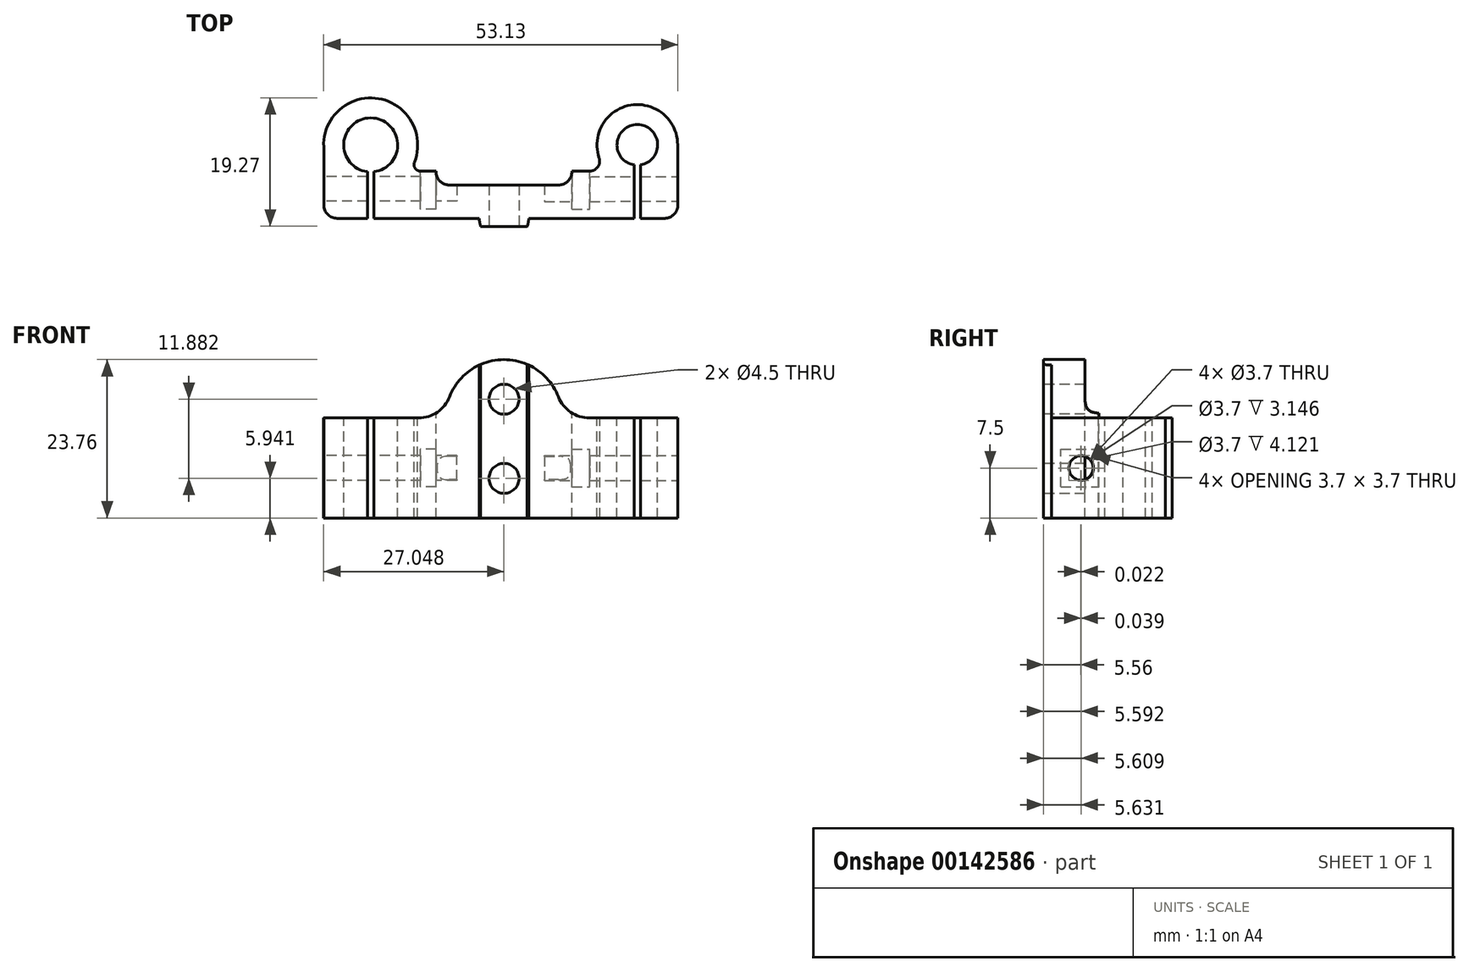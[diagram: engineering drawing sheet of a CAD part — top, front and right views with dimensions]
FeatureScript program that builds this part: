
annotation { "Feature Type Name" : "Feature", "Feature Type Description" : "" }
export const myFeature = defineFeature(function(context is Context, id is Id, definition is map)
    precondition{}
    {
        {
            var Q0;
            Q0=qCreatedBy(makeId("Top.planeOp"),FACE);
            var sketch = newSketch(context, id + "F0", { "sketchPlane" : qUnion([Q0])});
            skArc(sketch, "E0", {"start": v(12.6, -22.52) * mm, "mid": v(12.1, -16.46) * mm, "end": v(11.6, -22.52) * mm});
            skArc(sketch, "E1", {"start": v(-27.4, -23.53) * mm, "mid": v(-27.9, -15.46) * mm, "end": v(-28.4, -23.53) * mm});
            skArc(sketch, "E2", {"start": v(18.16, -19.49) * mm, "mid": v(11.1, -13.55) * mm, "end": v(6.38, -21.47) * mm});
            skArc(sketch, "E3", {"start": v(-21.33, -22.1) * mm, "mid": v(-26.72, -12.56) * mm, "end": v(-34.94, -19.8) * mm});
            skLineSegment(sketch, "E4", {"start": v(0.3, -25.53) * mm, "end": v(-16.08, -25.53) * mm});
            skLineSegment(sketch, "E5", {"start": v(-32.94, -30.53) * mm, "end": v(-28.4, -30.53) * mm});
            skLineSegment(sketch, "E6", {"start": v(-34.94, -19.8) * mm, "end": v(-34.94, -28.53) * mm});
            skPoint(sketch, "E7", {"position": v(-8.2, -30.53) * mm});
            skPoint(sketch, "E8", {"position": v(-8.2, -25.53) * mm});
            skLineSegment(sketch, "E9.rect.top", {"start": v(-27.4, -8.5) * mm, "end": v(-28.4, -8.5) * mm});
            skLineSegment(sketch, "E9.rect.left", {"start": v(-27.4, -30.53) * mm, "end": v(-27.4, -23.53) * mm});
            skLineSegment(sketch, "E9.rect.right", {"start": v(-28.4, -30.53) * mm, "end": v(-28.4, -23.53) * mm});
            skLineSegment(sketch, "E10.MirrorCS", {"start": v(-26.83, -5.34) * mm, "end": v(-27.83, -5.34) * mm});
            skLineSegment(sketch, "E11", {"start": v(-27.9, -19.51) * mm, "end": v(12.1, -19.51) * mm, "construction": true});
            skPoint(sketch, "E12", {"position": v(-7.9, -19.51) * mm});
            skLineSegment(sketch, "E13", {"start": v(-7.9, -19.51) * mm, "end": v(-7.9, -30.53) * mm, "construction": true});
            skLineSegment(sketch, "E14.MirrorCS", {"start": v(11.04, -5.34) * mm, "end": v(12.04, -5.34) * mm});
            skLineSegment(sketch, "E15.MirrorCS", {"start": v(12.6, -30.53) * mm, "end": v(12.6, -22.52) * mm});
            skLineSegment(sketch, "E16.MirrorCS", {"start": v(11.6, -30.53) * mm, "end": v(11.6, -22.52) * mm});
            skPoint(sketch, "E17.MirrorCS.end.orphan", {"position": v(12.6, -8.5) * mm});
            skPoint(sketch, "E18.orphan", {"position": v(11.6, -8.5) * mm});
            skPoint(sketch, "E19.MirrorCS.end.orphan", {"position": v(12.04, -5.34) * mm});
            skPoint(sketch, "E19.MirrorCS.start.orphan", {"position": v(11.04, -5.34) * mm});
            skLineSegment(sketch, "E20.trimOffspring", {"start": v(-27.4, -30.53) * mm, "end": v(-11.6, -30.53) * mm});
            skLineSegment(sketch, "E21.trimOffspring", {"start": v(12.6, -30.53) * mm, "end": v(16.2, -30.53) * mm});
            skLineSegment(sketch, "E22.filletArc", {"start": v(11.5, -25.53) * mm, "end": v(11.5, -25.53) * mm});
            skLineSegment(sketch, "E23.filletArc", {"start": v(-24.22, -25.53) * mm, "end": v(-24.22, -25.53) * mm});
            skPoint(sketch, "E24.orphan", {"position": v(18.12, -30.53) * mm});
            skLineSegment(sketch, "E25", {"start": v(18.2, -28.52) * mm, "end": v(18.16, -19.49) * mm});
            skPoint(sketch, "E26.orphan", {"position": v(-34.5, -30.53) * mm});
            skPoint(sketch, "E27.visualSharp", {"position": v(18.2, -30.53) * mm});
            skArc(sketch, "E27.filletArc", {"start": v(16.2, -30.53) * mm, "mid": v(17.61, -29.94) * mm, "end": v(18.2, -28.52) * mm});
            skPoint(sketch, "E28.visualSharp", {"position": v(-34.94, -30.53) * mm});
            skArc(sketch, "E28.filletArc", {"start": v(-34.94, -28.53) * mm, "mid": v(-34.35, -29.95) * mm, "end": v(-32.94, -30.53) * mm});
            skLineSegment(sketch, "E29.rect.bottom", {"start": v(-18.08, -28.96) * mm, "end": v(-20.58, -28.96) * mm});
            skLineSegment(sketch, "E29.rect.left", {"start": v(-18.08, -28.96) * mm, "end": v(-18.08, -25.53) * mm});
            skLineSegment(sketch, "E29.rect.right", {"start": v(-20.58, -28.96) * mm, "end": v(-20.58, -25.53) * mm});
            skPoint(sketch, "E29.rect.middle", {"position": v(-19.33, -26.2) * mm});
            skLineSegment(sketch, "E30.MirrorCS", {"start": v(4.8, -28.96) * mm, "end": v(4.8, -25.53) * mm});
            skLineSegment(sketch, "E31.MirrorCS", {"start": v(2.3, -28.96) * mm, "end": v(2.3, -25.53) * mm});
            skLineSegment(sketch, "E32.MirrorCS", {"start": v(2.3, -28.96) * mm, "end": v(4.8, -28.96) * mm});
            skPoint(sketch, "E33.MirrorP", {"position": v(3.55, -26.2) * mm});
            skPoint(sketch, "E34", {"position": v(-27.4, -27.03) * mm});
            skPoint(sketch, "E35.orphan", {"position": v(-20.58, -23.46) * mm});
            skPoint(sketch, "E36.orphan", {"position": v(-18.08, -23.46) * mm});
            skPoint(sketch, "E37.MirrorCS.end.orphan", {"position": v(4.8, -23.46) * mm});
            skPoint(sketch, "E37.MirrorCS.start.orphan", {"position": v(2.3, -23.46) * mm});
            skLineSegment(sketch, "E38", {"start": v(-20.58, -25.53) * mm, "end": v(-20.58, -23.46) * mm});
            skLineSegment(sketch, "E39", {"start": v(-18.08, -23.46) * mm, "end": v(-18.08, -23.53) * mm});
            skLineSegment(sketch, "E40", {"start": v(-20.4, -23.46) * mm, "end": v(-18.08, -23.46) * mm});
            skLineSegment(sketch, "E41", {"start": v(2.3, -23.46) * mm, "end": v(4.96, -23.46) * mm});
            skLineSegment(sketch, "E42", {"start": v(4.8, -25.53) * mm, "end": v(4.8, -23.46) * mm});
            skLineSegment(sketch, "E43", {"start": v(2.3, -23.46) * mm, "end": v(2.3, -23.53) * mm});
            skLineSegment(sketch, "E44.filletArc", {"start": v(-22.05, -23.46) * mm, "end": v(-22.05, -23.46) * mm});
            skLineSegment(sketch, "E45.filletArc", {"start": v(7.52, -23.46) * mm, "end": v(7.52, -23.46) * mm});
            skArc(sketch, "E46.filletArc", {"start": v(-21.33, -22.1) * mm, "mid": v(-21.23, -23.02) * mm, "end": v(-20.4, -23.46) * mm});
            skArc(sketch, "E47.filletArc", {"start": v(4.96, -23.46) * mm, "mid": v(6.18, -22.83) * mm, "end": v(6.38, -21.47) * mm});
            skArc(sketch, "E48.filletArc", {"start": v(-18.08, -23.53) * mm, "mid": v(-17.5, -24.95) * mm, "end": v(-16.08, -25.53) * mm});
            skArc(sketch, "E49.filletArc", {"start": v(0.3, -25.53) * mm, "mid": v(1.71, -24.95) * mm, "end": v(2.3, -23.53) * mm});
            skArc(sketch, "E50", {"start": v(-11.6, -30.53) * mm, "mid": v(-11.54, -31.14) * mm, "end": v(-11.4, -31.73) * mm});
            skLineSegment(sketch, "E51.trimOffspring", {"start": v(-4.2, -30.53) * mm, "end": v(11.6, -30.53) * mm});
            skLineSegment(sketch, "E52", {"start": v(-4.4, -31.73) * mm, "end": v(-11.4, -31.73) * mm});
            skArc(sketch, "E53.trimOffspring", {"start": v(-4.4, -31.73) * mm, "mid": v(-4.24, -31.14) * mm, "end": v(-4.2, -30.53) * mm});
            skSolve(sketch);
        }
        {
            var Q0;
            Q0=qSketchRegion(id+"F0",true);
            var Q1;
            Q1=makeQuery(id+"F0.imprint","IMPRINT",FACE,{"disambiguationData":[TD([[makeQuery(id+"F0.imprint","IMPRINT",EDGE,{"derivedFrom":sQuery(id+"F0.wireOp",EDGE,"E0")}),-1.0]])]});
            extrude(context, id + "F1", {"entities" : qUnion([Q0, Q1]), "oppositeDirection" : true, "depth" : 15 * mm});
        }
        {
            var Q0;
            Q0=qCreatedBy(makeId("Right.planeOp"),FACE);
            var sketch = newSketch(context, id + "F2", { "sketchPlane" : qUnion([Q0])});
            skLineSegment(sketch, "E54.0.0", {"start": v(-19.49, 0) * mm, "end": v(-28.52, 0) * mm});
            skLineSegment(sketch, "E54.0.1", {"start": v(-28.52, 0) * mm, "end": v(-28.52, -15) * mm});
            skLineSegment(sketch, "E54.0.2", {"start": v(-28.52, -15) * mm, "end": v(-19.49, -15) * mm});
            skLineSegment(sketch, "E54.0.3", {"start": v(-19.49, -15) * mm, "end": v(-19.49, 0) * mm});
            skLineSegment(sketch, "E54.1.0", {"start": v(-28.52, 0) * mm, "end": v(-30.53, 0) * mm});
            skLineSegment(sketch, "E54.1.1", {"start": v(-30.53, 0) * mm, "end": v(-30.53, -15) * mm});
            skLineSegment(sketch, "E54.1.2", {"start": v(-30.53, -15) * mm, "end": v(-28.52, -15) * mm});
            skLineSegment(sketch, "E54.1.3", {"start": v(-28.52, -15) * mm, "end": v(-28.52, 0) * mm});
            skPoint(sketch, "E55", {"position": v(-19.49, -7.5) * mm});
            skLineSegment(sketch, "E56", {"start": v(-19.49, -7.5) * mm, "end": v(-30.53, -7.5) * mm});
            skPoint(sketch, "E57", {"position": v(-26.2, -7.5) * mm});
            skPoint(sketch, "E58", {"position": v(-29.45, -48.71) * mm});
            skPoint(sketch, "E59", {"position": v(-22.93, -48.71) * mm});
            skPoint(sketch, "E60.trimOffspring.end.orphan", {"position": v(-22.59, -47.18) * mm});
            skPoint(sketch, "E61.trimOffspring.start.orphan", {"position": v(-29.79, -47.18) * mm});
            skSolve(sketch);
        }
        {
            var Q0;
            Q0=makeQuery(id+"F1.opExtrude","SWEPT_FACE",FACE,{"disambiguationData":[OSD([sQuery(id+"F0.wireOp",EDGE,"E25")])]});
            var sketch = newSketch(context, id + "F3", { "sketchPlane" : qUnion([Q0])});
            skPoint(sketch, "E62", {"position": v(-28.96, -7.5) * mm});
            skPoint(sketch, "E63", {"position": v(-37.59, 27.7) * mm});
            skPoint(sketch, "E64", {"position": v(-31.07, 27.7) * mm});
            skPoint(sketch, "E65.trimOffspring.end.orphan", {"position": v(-30.73, 29.23) * mm});
            skPoint(sketch, "E66.start.orphan", {"position": v(-37.93, 29.23) * mm});
            skPoint(sketch, "E67", {"position": v(-23.46, -7.5) * mm});
            skLineSegment(sketch, "E68", {"start": v(-28.9, -7.5) * mm, "end": v(-28.96, -7.5) * mm});
            skLineSegment(sketch, "E69", {"start": v(-23.44, -7.5) * mm, "end": v(-23.46, -7.5) * mm});
            skPoint(sketch, "E70", {"position": v(-26.17, -7.5) * mm});
            skCircle(sketch, "E71", {"center": v(-26.17, -7.5) * mm, "radius": 1.85 * mm});
            skPoint(sketch, "E72.0.start.orphan", {"position": v(-19.49, -7.5) * mm});
            skPoint(sketch, "E73.orphan", {"position": v(-30.53, -7.5) * mm});
            skSolve(sketch);
        }
        {
            var Q0;
            Q0=makeQuery(id+"F1.opExtrude","SWEPT_FACE",FACE,{"disambiguationData":[OSD([sQuery(id+"F0.wireOp",EDGE,"E6")])]});
            var sketch = newSketch(context, id + "F4", { "sketchPlane" : qUnion([Q0])});
            skEllipse(sketch, "E74.0", {"center": v(26.1, -7.5) * mm, "majorRadius": 1.85 * mm, "minorRadius": 1.85 * mm, "majorAxis": v(0, 1)});
            skSolve(sketch);
        }
        {
            var Q0;
            Q0=makeQuery(id+"F4.imprint","IMPRINT",FACE,{"disambiguationData":[TD([[makeQuery(id+"F4.imprint","IMPRINT",EDGE,{"derivedFrom":sQuery(id+"F4.wireOp",EDGE,"E74.0")}),1.0]])]});
            extrude(context, id + "F5", {"entities" : qUnion([Q0]), "operationType" : NewBodyOperationType.REMOVE, "oppositeDirection" : true, "depth" : 20 * mm});
        }
        {
            var Q0;
            Q0=qSketchRegion(id+"F3",true);
            var Q1;
            Q1=makeQuery(id+"F3.imprint","IMPRINT",FACE,{"disambiguationData":[TD([[makeQuery(id+"F3.imprint","IMPRINT",EDGE,{"derivedFrom":sQuery(id+"F3.wireOp",EDGE,"E71")}),1.0]])]});
            extrude(context, id + "F6", {"entities" : qUnion([Q0, Q1]), "operationType" : NewBodyOperationType.REMOVE, "oppositeDirection" : true, "depth" : 20 * mm});
        }
        {
            var Q0;
            Q0=makeQuery(id+"F1.opExtrude","SWEPT_FACE",FACE,{"disambiguationData":[OSD([sQuery(id+"F0.wireOp",EDGE,"E41")])]});
            var sketch = newSketch(context, id + "F7", { "sketchPlane" : qUnion([Q0])});
            skLineSegment(sketch, "E75", {"start": v(-2.3, -7.5) * mm, "end": v(-4.96, -7.5) * mm});
            skPoint(sketch, "E76", {"position": v(-3.63, -7.5) * mm});
            skLineSegment(sketch, "E77.rect.bottom", {"start": v(-2.3, -10.35) * mm, "end": v(-4.96, -10.35) * mm});
            skLineSegment(sketch, "E77.rect.top", {"start": v(-2.3, -4.65) * mm, "end": v(-4.96, -4.65) * mm});
            skLineSegment(sketch, "E77.rect.left", {"start": v(-2.3, -10.35) * mm, "end": v(-2.3, -4.65) * mm});
            skLineSegment(sketch, "E77.rect.right", {"start": v(-4.96, -10.35) * mm, "end": v(-4.96, -4.65) * mm});
            skLineSegment(sketch, "E78.0.0", {"start": v(20.4, 0) * mm, "end": v(18.08, 0) * mm});
            skLineSegment(sketch, "E78.0.1", {"start": v(18.08, 0) * mm, "end": v(18.08, -15) * mm});
            skLineSegment(sketch, "E78.0.2", {"start": v(18.08, -15) * mm, "end": v(20.4, -15) * mm});
            skLineSegment(sketch, "E78.0.3", {"start": v(20.4, -15) * mm, "end": v(20.4, 0) * mm});
            skLineSegment(sketch, "E79", {"start": v(-2.3, -7.5) * mm, "end": v(18.08, -7.5) * mm});
            skPoint(sketch, "E80", {"position": v(7.9, -7.5) * mm});
            skLineSegment(sketch, "E81", {"start": v(7.9, -7.5) * mm, "end": v(7.9, -15.38) * mm, "construction": true});
            skPoint(sketch, "E82.MirrorP", {"position": v(19.42, -7.5) * mm});
            skLineSegment(sketch, "E83.MirrorCS", {"start": v(18.08, -7.5) * mm, "end": v(20.75, -7.5) * mm});
            skLineSegment(sketch, "E84.MirrorCS", {"start": v(18.08, -10.35) * mm, "end": v(20.75, -10.35) * mm});
            skLineSegment(sketch, "E85.MirrorCS", {"start": v(18.08, -4.65) * mm, "end": v(20.75, -4.65) * mm});
            skLineSegment(sketch, "E86.MirrorCS", {"start": v(18.08, -10.35) * mm, "end": v(18.08, -4.65) * mm});
            skLineSegment(sketch, "E87.MirrorCS", {"start": v(18.08, -7.5) * mm, "end": v(-2.3, -7.5) * mm});
            skLineSegment(sketch, "E88.MirrorCS", {"start": v(20.75, -10.35) * mm, "end": v(20.75, -4.65) * mm});
            skSolve(sketch);
        }
        {
            var Q0;
            {var subQ0=sQuery(id+"F7.wireOp",EDGE,"E75");Q0=makeQuery(id+"F7.imprint","IMPRINT",FACE,{"disambiguationData":[TD([[makeQuery(id+"F7.imprint","IMPRINT",EDGE,{"derivedFrom":subQ0}),-1.0]])]});}
            var Q1;
            {var subQ0=sQuery(id+"F7.wireOp",EDGE,"E84.MirrorCS");var subQ1=sQuery(id+"F7.wireOp",EDGE,"E78.0.3");var subQ2=makeQuery(id+"F7.imprint","INTERSECT",VERTEX,{"derivedFrom":[subQ1,subQ0]});Q1=makeQuery(id+"F7.imprint","IMPRINT",FACE,{"disambiguationData":[TD([[makeQuery(id+"F7.imprint","IMPRINT",EDGE,{"disambiguationData":[TD([[subQ2,-1.0]])],"derivedFrom":subQ1}),1.0]])]});}
            var Q2;
            {var subQ0=sQuery(id+"F7.wireOp",EDGE,"E85.MirrorCS");var subQ1=sQuery(id+"F7.wireOp",EDGE,"E78.0.3");var subQ2=makeQuery(id+"F7.imprint","INTERSECT",VERTEX,{"derivedFrom":[subQ1,subQ0]});Q2=makeQuery(id+"F7.imprint","IMPRINT",FACE,{"disambiguationData":[TD([[makeQuery(id+"F7.imprint","IMPRINT",EDGE,{"disambiguationData":[TD([[subQ2,1.0]])],"derivedFrom":subQ1}),1.0]])]});}
            var Q3;
            {var subQ0=sQuery(id+"F7.wireOp",EDGE,"E75");Q3=makeQuery(id+"F7.imprint","IMPRINT",FACE,{"disambiguationData":[TD([[makeQuery(id+"F7.imprint","IMPRINT",EDGE,{"derivedFrom":subQ0}),1.0]])]});}
            extrude(context, id + "F8", {"entities" : qUnion([Q0, Q1, Q2, Q3]), "operationType" : NewBodyOperationType.REMOVE, "oppositeDirection" : true, "depth" : 5.7 * mm});
        }
        {
            var Q0;
            Q0=makeQuery(id+"F1.opExtrude","SWEPT_FACE",FACE,{"disambiguationData":[OSD([sQuery(id+"F0.wireOp",EDGE,"E20.trimOffspring")])]});
            var sketch = newSketch(context, id + "F9", { "sketchPlane" : qUnion([Q0])});
            skLineSegment(sketch, "E89.0.0", {"start": v(11.6, 0) * mm, "end": v(-4.2, 0) * mm});
            skLineSegment(sketch, "E89.0.1", {"start": v(-4.2, 0) * mm, "end": v(-4.2, -15) * mm});
            skLineSegment(sketch, "E89.0.2", {"start": v(-4.2, -15) * mm, "end": v(11.6, -15) * mm});
            skLineSegment(sketch, "E89.0.3", {"start": v(11.6, -15) * mm, "end": v(11.6, 0) * mm});
            skLineSegment(sketch, "E90", {"start": v(11.6, 0) * mm, "end": v(4.93, 0) * mm});
            skPoint(sketch, "E91", {"position": v(-7.9, 0) * mm});
            skArc(sketch, "E92", {"start": v(0.27, 3.18) * mm, "mid": v(-7.9, 8.76) * mm, "end": v(-16.06, 3.18) * mm});
            skLineSegment(sketch, "E93.trimOffspring", {"start": v(-20.72, 0) * mm, "end": v(-27.4, 0) * mm});
            skPoint(sketch, "E94.visualSharp", {"position": v(-16.66, 0) * mm});
            skArc(sketch, "E94.filletArc", {"start": v(-20.72, 0) * mm, "mid": v(-17.9, 0.87) * mm, "end": v(-16.06, 3.18) * mm});
            skPoint(sketch, "E95.visualSharp", {"position": v(0.87, 0) * mm});
            skArc(sketch, "E95.filletArc", {"start": v(0.27, 3.18) * mm, "mid": v(2.11, 0.87) * mm, "end": v(4.93, 0) * mm});
            skLineSegment(sketch, "E96", {"start": v(-20.72, 0) * mm, "end": v(4.93, 0) * mm});
            skSolve(sketch);
        }
        {
            var Q0;
            Q0=makeQuery(id+"F9.imprint","IMPRINT",FACE,{"disambiguationData":[TD([[makeQuery(id+"F9.imprint","IMPRINT",EDGE,{"derivedFrom":sQuery(id+"F9.wireOp",EDGE,"E92")}),1.0]])]});
            var Q1;
            Q1=makeQuery(id+"F1.opExtrude","SWEPT_FACE",FACE,{"disambiguationData":[OSD([sQuery(id+"F0.wireOp",EDGE,"E4")])]});
            extrude(context, id + "F10", {"entities" : qUnion([Q0]), "operationType" : NewBodyOperationType.ADD, "endBound" : BoundingType.UP_TO_SURFACE, "oppositeDirection" : true, "endBoundEntityFace" : qUnion([Q1]), "depth" : 25 * mm});
        }
        {
            var Q0;
            {var subQ0=sQuery(id+"F0.wireOp",EDGE,"E51.trimOffspring");var subQ1=sQuery(id+"F0.wireOp",EDGE,"E50");var subQ2=sQuery(id+"F0.wireOp",EDGE,"E52");var subQ3=sQuery(id+"F0.wireOp",EDGE,"E20.trimOffspring");var subQ4=sQuery(id+"F0.wireOp",EDGE,"E53.trimOffspring");Q0=makeQuery(id+"F10.boolean.opBoolean","SPLIT",FACE,{"disambiguationData":[TD([makeQuery(id+"F1.opExtrude","SWEPT_FACE",FACE,{"disambiguationData":[OSD([subQ1])]})])],"derivedFrom":makeQuery(id+"F1.opExtrude","CAP_FACE",FACE,{"disambiguationData":[OSD([sQuery(id+"F0.wireOp",EDGE,"E0"),sQuery(id+"F0.wireOp",EDGE,"E1"),sQuery(id+"F0.wireOp",EDGE,"E2"),sQuery(id+"F0.wireOp",EDGE,"E3"),sQuery(id+"F0.wireOp",EDGE,"E4"),sQuery(id+"F0.wireOp",EDGE,"E5"),sQuery(id+"F0.wireOp",EDGE,"E6"),sQuery(id+"F0.wireOp",EDGE,"E9.rect.left"),sQuery(id+"F0.wireOp",EDGE,"E9.rect.right"),sQuery(id+"F0.wireOp",EDGE,"E15.MirrorCS"),sQuery(id+"F0.wireOp",EDGE,"E16.MirrorCS"),subQ3,sQuery(id+"F0.wireOp",EDGE,"E21.trimOffspring"),sQuery(id+"F0.wireOp",EDGE,"E25"),sQuery(id+"F0.wireOp",EDGE,"E27.filletArc"),sQuery(id+"F0.wireOp",EDGE,"E28.filletArc"),sQuery(id+"F0.wireOp",EDGE,"E39"),sQuery(id+"F0.wireOp",EDGE,"E40"),sQuery(id+"F0.wireOp",EDGE,"E41"),sQuery(id+"F0.wireOp",EDGE,"E43"),sQuery(id+"F0.wireOp",EDGE,"E46.filletArc"),sQuery(id+"F0.wireOp",EDGE,"E47.filletArc"),sQuery(id+"F0.wireOp",EDGE,"E48.filletArc"),sQuery(id+"F0.wireOp",EDGE,"E49.filletArc"),subQ1,subQ0,subQ2,subQ4])],"isStart":true})});}
            var Q1;
            Q1=makeQuery(id+"F10.opExtrude","SWEPT_FACE",FACE,{"disambiguationData":[OSD([sQuery(id+"F9.wireOp",EDGE,"E92")])]});
            extrude(context, id + "F11", {"entities" : qUnion([Q0]), "operationType" : NewBodyOperationType.ADD, "endBound" : BoundingType.UP_TO_SURFACE, "endBoundEntityFace" : qUnion([Q1]), "depth" : 25 * mm});
        }
        {
            var Q0;
            {var subQ0=sQuery(id+"F0.wireOp",EDGE,"E52");Q0=makeQuery(id+"F11.boolean.opBoolean","MERGE",FACE,{"derivedFrom":[makeQuery(id+"F1.opExtrude","SWEPT_FACE",FACE,{"disambiguationData":[OSD([subQ0])]}),makeQuery(id+"F11.opExtrude","SWEPT_FACE",FACE,{"disambiguationData":[OSD([subQ0])]})]});}
            var sketch = newSketch(context, id + "F12", { "sketchPlane" : qUnion([Q0])});
            skLineSegment(sketch, "E97", {"start": v(-7.9, -15) * mm, "end": v(-7.9, -9.06) * mm});
            skPoint(sketch, "E98", {"position": v(-7.9, -3.12) * mm});
            skLineSegment(sketch, "E99", {"start": v(-7.9, -3.12) * mm, "end": v(-7.9, 2.82) * mm});
            skLineSegment(sketch, "E100", {"start": v(-7.9, 2.82) * mm, "end": v(-7.9, 8.76) * mm});
            skLineSegment(sketch, "E101", {"start": v(-7.9, -9.06) * mm, "end": v(-7.9, -3.12) * mm});
            skSolve(sketch);
        }
        {
            var Q0;
            Q0=sQuery(id+"F12.wireOp",VERTEX,"E100.start");
            var Q1;
            Q1=sQuery(id+"F12.wireOp",VERTEX,"E101.start");
            var Q2;
            Q2=makeQuery(id+"F1.opExtrude","SWEPT_BODY",BODY,{"disambiguationData":[OSD([sQuery(id+"F0.wireOp",EDGE,"E0"),sQuery(id+"F0.wireOp",EDGE,"E1"),sQuery(id+"F0.wireOp",EDGE,"E2"),sQuery(id+"F0.wireOp",EDGE,"E3"),sQuery(id+"F0.wireOp",EDGE,"E4"),sQuery(id+"F0.wireOp",EDGE,"E5"),sQuery(id+"F0.wireOp",EDGE,"E6"),sQuery(id+"F0.wireOp",EDGE,"E9.rect.left"),sQuery(id+"F0.wireOp",EDGE,"E9.rect.right"),sQuery(id+"F0.wireOp",EDGE,"E15.MirrorCS"),sQuery(id+"F0.wireOp",EDGE,"E16.MirrorCS"),sQuery(id+"F0.wireOp",EDGE,"E20.trimOffspring"),sQuery(id+"F0.wireOp",EDGE,"E21.trimOffspring"),sQuery(id+"F0.wireOp",EDGE,"E25"),sQuery(id+"F0.wireOp",EDGE,"E27.filletArc"),sQuery(id+"F0.wireOp",EDGE,"E28.filletArc"),sQuery(id+"F0.wireOp",EDGE,"E39"),sQuery(id+"F0.wireOp",EDGE,"E40"),sQuery(id+"F0.wireOp",EDGE,"E41"),sQuery(id+"F0.wireOp",EDGE,"E43"),sQuery(id+"F0.wireOp",EDGE,"E46.filletArc"),sQuery(id+"F0.wireOp",EDGE,"E47.filletArc"),sQuery(id+"F0.wireOp",EDGE,"E48.filletArc"),sQuery(id+"F0.wireOp",EDGE,"E49.filletArc"),sQuery(id+"F0.wireOp",EDGE,"E50"),sQuery(id+"F0.wireOp",EDGE,"E51.trimOffspring"),sQuery(id+"F0.wireOp",EDGE,"E52"),sQuery(id+"F0.wireOp",EDGE,"E53.trimOffspring")])]});
            hole(context, id + "F13", {"style" : HoleStyle.SIMPLE, "holeDiameter" : 4.5 * mm, "endStyle" : HoleEndStyle.THROUGH, "locations" : qUnion([Q0, Q1]), "scope" : qUnion([Q2])});
        }
        {
            var Q0;
            {var subQ0=sQuery(id+"F0.wireOp",EDGE,"E41");var subQ1=sQuery(id+"F0.wireOp",EDGE,"E20.trimOffspring");var subQ2=sQuery(id+"F0.wireOp",EDGE,"E25");var subQ3=sQuery(id+"F0.wireOp",EDGE,"E21.trimOffspring");var subQ4=sQuery(id+"F0.wireOp",EDGE,"E43");var subQ9=sQuery(id+"F0.wireOp",EDGE,"E16.MirrorCS");var subQ10=sQuery(id+"F0.wireOp",EDGE,"E0");var subQ11=sQuery(id+"F0.wireOp",EDGE,"E27.filletArc");var subQ12=sQuery(id+"F0.wireOp",EDGE,"E2");var subQ13=sQuery(id+"F0.wireOp",EDGE,"E4");var subQ14=sQuery(id+"F0.wireOp",EDGE,"E47.filletArc");var subQ15=sQuery(id+"F0.wireOp",EDGE,"E15.MirrorCS");var subQ16=sQuery(id+"F0.wireOp",EDGE,"E49.filletArc");var subQ17=sQuery(id+"F0.wireOp",EDGE,"E51.trimOffspring");Q0=makeQuery(id+"F10.boolean.opBoolean","SPLIT",FACE,{"disambiguationData":[TD([makeQuery(id+"F1.opExtrude","SWEPT_FACE",FACE,{"disambiguationData":[OSD([subQ10])]})])],"derivedFrom":makeQuery(id+"F1.opExtrude","CAP_FACE",FACE,{"disambiguationData":[OSD([subQ10,sQuery(id+"F0.wireOp",EDGE,"E1"),subQ12,sQuery(id+"F0.wireOp",EDGE,"E3"),subQ13,sQuery(id+"F0.wireOp",EDGE,"E5"),sQuery(id+"F0.wireOp",EDGE,"E6"),sQuery(id+"F0.wireOp",EDGE,"E9.rect.left"),sQuery(id+"F0.wireOp",EDGE,"E9.rect.right"),subQ15,subQ9,subQ1,subQ3,subQ2,subQ11,sQuery(id+"F0.wireOp",EDGE,"E28.filletArc"),sQuery(id+"F0.wireOp",EDGE,"E39"),sQuery(id+"F0.wireOp",EDGE,"E40"),subQ0,subQ4,sQuery(id+"F0.wireOp",EDGE,"E46.filletArc"),subQ14,sQuery(id+"F0.wireOp",EDGE,"E48.filletArc"),subQ16,sQuery(id+"F0.wireOp",EDGE,"E50"),subQ17,sQuery(id+"F0.wireOp",EDGE,"E52"),sQuery(id+"F0.wireOp",EDGE,"E53.trimOffspring")])],"isStart":true})});}
            var Q1;
            Q1=makeQuery(id+"F10.opExtrude","SWEPT_FACE",FACE,{"disambiguationData":[OSD([sQuery(id+"F9.wireOp",EDGE,"E95.filletArc")])]});
            extrude(context, id + "F14", {"entities" : qUnion([Q0]), "operationType" : NewBodyOperationType.ADD, "endBound" : BoundingType.UP_TO_SURFACE, "endBoundEntityFace" : qUnion([Q1]), "depth" : 25 * mm});
        }
        {
            var Q0;
            {var subQ0=sQuery(id+"F0.wireOp",EDGE,"E20.trimOffspring");var subQ1=sQuery(id+"F0.wireOp",EDGE,"E40");var subQ2=sQuery(id+"F0.wireOp",EDGE,"E28.filletArc");var subQ3=sQuery(id+"F0.wireOp",EDGE,"E9.rect.right");var subQ4=sQuery(id+"F0.wireOp",EDGE,"E51.trimOffspring");var subQ5=sQuery(id+"F0.wireOp",EDGE,"E9.rect.left");var subQ6=sQuery(id+"F0.wireOp",EDGE,"E6");var subQ8=sQuery(id+"F0.wireOp",EDGE,"E1");var subQ12=sQuery(id+"F0.wireOp",EDGE,"E3");var subQ13=sQuery(id+"F0.wireOp",EDGE,"E39");var subQ14=sQuery(id+"F0.wireOp",EDGE,"E4");var subQ15=sQuery(id+"F0.wireOp",EDGE,"E48.filletArc");var subQ16=sQuery(id+"F0.wireOp",EDGE,"E5");var subQ17=sQuery(id+"F0.wireOp",EDGE,"E46.filletArc");Q0=makeQuery(id+"F10.boolean.opBoolean","SPLIT",FACE,{"disambiguationData":[TD([makeQuery(id+"F1.opExtrude","SWEPT_FACE",FACE,{"disambiguationData":[OSD([subQ8])]})])],"derivedFrom":makeQuery(id+"F1.opExtrude","CAP_FACE",FACE,{"disambiguationData":[OSD([sQuery(id+"F0.wireOp",EDGE,"E0"),subQ8,sQuery(id+"F0.wireOp",EDGE,"E2"),subQ12,subQ14,subQ16,subQ6,subQ5,subQ3,sQuery(id+"F0.wireOp",EDGE,"E15.MirrorCS"),sQuery(id+"F0.wireOp",EDGE,"E16.MirrorCS"),subQ0,sQuery(id+"F0.wireOp",EDGE,"E21.trimOffspring"),sQuery(id+"F0.wireOp",EDGE,"E25"),sQuery(id+"F0.wireOp",EDGE,"E27.filletArc"),subQ2,subQ13,subQ1,sQuery(id+"F0.wireOp",EDGE,"E41"),sQuery(id+"F0.wireOp",EDGE,"E43"),subQ17,sQuery(id+"F0.wireOp",EDGE,"E47.filletArc"),subQ15,sQuery(id+"F0.wireOp",EDGE,"E49.filletArc"),sQuery(id+"F0.wireOp",EDGE,"E50"),subQ4,sQuery(id+"F0.wireOp",EDGE,"E52"),sQuery(id+"F0.wireOp",EDGE,"E53.trimOffspring")])],"isStart":true})});}
            var Q1;
            Q1=makeQuery(id+"F10.opExtrude","SWEPT_FACE",FACE,{"disambiguationData":[OSD([sQuery(id+"F9.wireOp",EDGE,"E94.filletArc")])]});
            extrude(context, id + "F15", {"entities" : qUnion([Q0]), "operationType" : NewBodyOperationType.ADD, "endBound" : BoundingType.UP_TO_SURFACE, "endBoundEntityFace" : qUnion([Q1]), "depth" : 25 * mm});
        }
    });
